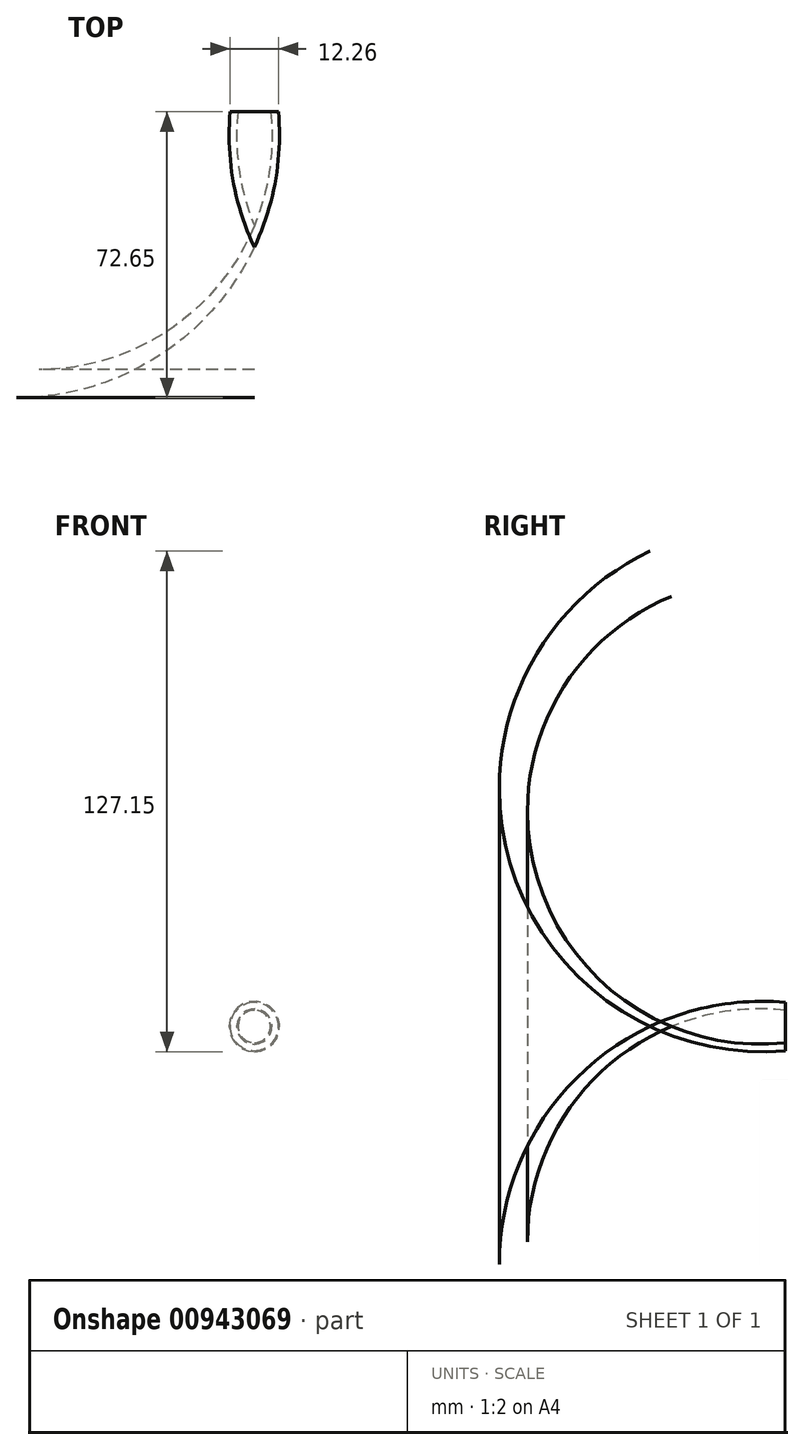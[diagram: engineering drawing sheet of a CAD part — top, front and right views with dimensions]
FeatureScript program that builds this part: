
annotation { "Feature Type Name" : "Feature", "Feature Type Description" : "" }
export const myFeature = defineFeature(function(context is Context, id is Id, definition is map)
    precondition{}
    {
        {
            var Q0;
            Q0=qCreatedBy(makeId("Right.planeOp"),FACE);
            var sketch = newSketch(context, id + "F0", { "sketchPlane" : qUnion([Q0])});
            skPoint(sketch, "E0.start.orphan", {"position": v(0, 40.3) * mm});
            skLineSegment(sketch, "E1", {"start": v(0, 12.26) * mm, "end": v(0, 0) * mm});
            skLineSegment(sketch, "E2", {"start": v(0, 6.13) * mm, "end": v(-34.38, 6.13) * mm});
            skArc(sketch, "E3", {"start": v(-34.38, 6.13) * mm, "mid": v(-17.6, 0.78) * mm, "end": v(0, 0) * mm});
            skArc(sketch, "E4", {"start": v(-28.93, 6.13) * mm, "mid": v(-14.73, 2.25) * mm, "end": v(0, 2) * mm});
            skSolve(sketch);
        }
        {
            var Q0;
            Q0=qCreatedBy(makeId("Front.planeOp"),FACE);
            var sketch = newSketch(context, id + "F1", { "sketchPlane" : qUnion([Q0])});
            skLineSegment(sketch, "E5.0", {"start": v(0, 12.26) * mm, "end": v(0, 0) * mm});
            skPoint(sketch, "E6.0", {"position": v(0, 6.13) * mm});
            skCircle(sketch, "E7", {"center": v(0, 6.13) * mm, "radius": 6.13 * mm});
            skSolve(sketch);
        }
        {
            var Q0;
            {var subQ0=sQuery(id+"F0.wireOp",EDGE,"E3");Q0=makeQuery(id+"F0.imprint","IMPRINT",FACE,{"disambiguationData":[TD([[makeQuery(id+"F0.imprint","IMPRINT",EDGE,{"derivedFrom":subQ0}),1.0]])]});}
            var Q1;
            Q1=sQuery(id+"F1.wireOp",EDGE,"E7");
            revolve(context, id + "F2", {"surfaceOperationType" : NewSurfaceOperationType.NEW, "entities" : qUnion([Q0]), "axis" : qUnion([Q1]), "revolveType" : RevolveType.FULL});
        }
    });
